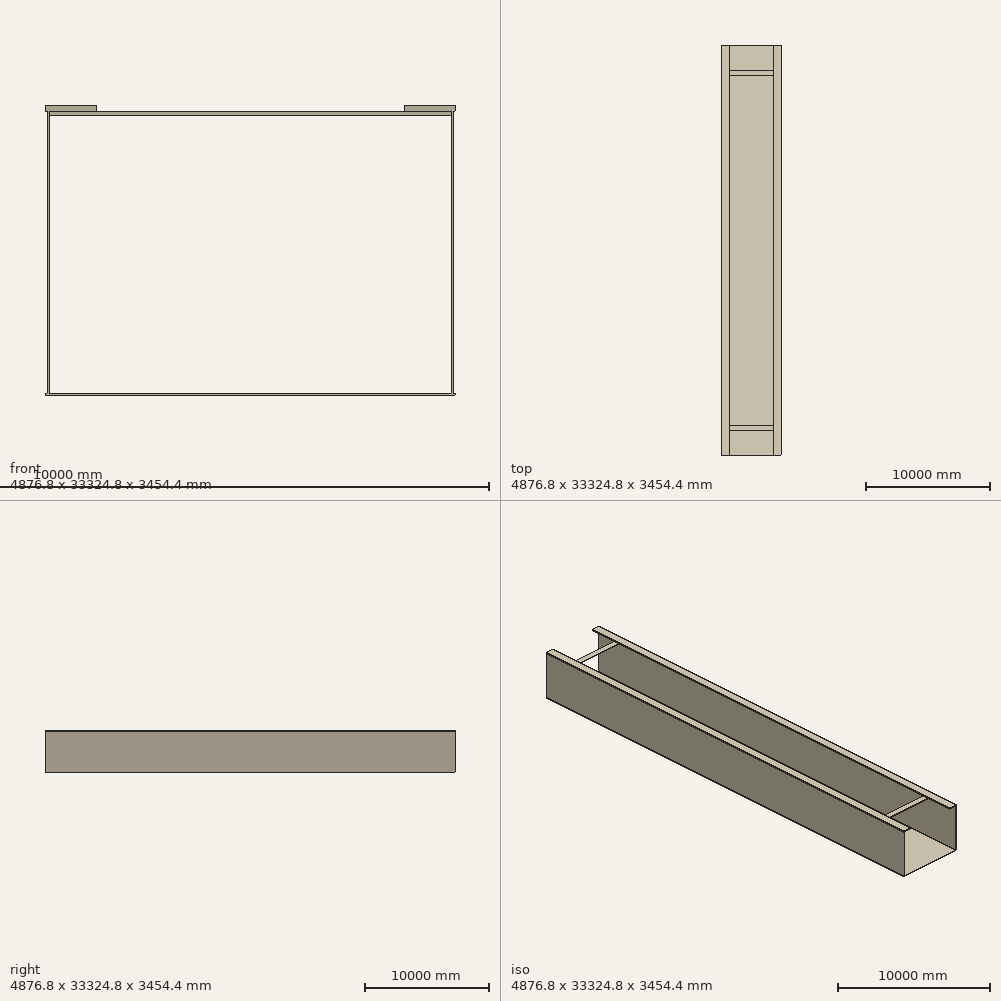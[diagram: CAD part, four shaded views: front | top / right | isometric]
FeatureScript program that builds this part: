
annotation { "Feature Type Name" : "Feature", "Feature Type Description" : "" }
export const myFeature = defineFeature(function(context is Context, id is Id, definition is map)
    precondition{}
    {
        {
            var Q0;
            Q0=qCreatedBy(makeId("Front.planeOp"),FACE);
            var sketch = newSketch(context, id + "F0", { "sketchPlane" : qUnion([Q0])});
            skLineSegment(sketch, "E0.bottom", {"start": v(0, 0) * mm, "end": v(4876.8, 0) * mm});
            skLineSegment(sketch, "E0.top", {"start": v(0, 25.4) * mm, "end": v(4876.8, 25.4) * mm});
            skLineSegment(sketch, "E0.left", {"start": v(0, 0) * mm, "end": v(0, 25.4) * mm});
            skLineSegment(sketch, "E0.right", {"start": v(4876.8, 0) * mm, "end": v(4876.8, 25.4) * mm});
            skLineSegment(sketch, "E1.left", {"start": v(4826, 25.4) * mm, "end": v(4826, 3378.2) * mm});
            skLineSegment(sketch, "E1.right", {"start": v(4851.4, 25.4) * mm, "end": v(4851.4, 3378.2) * mm});
            skLineSegment(sketch, "E2.bottom", {"start": v(25.4, 25.4) * mm, "end": v(50.8, 25.4) * mm});
            skLineSegment(sketch, "E2.top", {"start": v(25.4, 3378.2) * mm, "end": v(50.8, 3378.2) * mm});
            skLineSegment(sketch, "E2.left", {"start": v(25.4, 25.4) * mm, "end": v(25.4, 3378.2) * mm});
            skLineSegment(sketch, "E2.right", {"start": v(50.8, 25.4) * mm, "end": v(50.8, 3378.2) * mm});
            skLineSegment(sketch, "E3.bottom", {"start": v(0, 3378.2) * mm, "end": v(609.6, 3378.2) * mm});
            skLineSegment(sketch, "E3.top", {"start": v(0, 3454.4) * mm, "end": v(609.6, 3454.4) * mm});
            skLineSegment(sketch, "E3.left", {"start": v(0, 3378.2) * mm, "end": v(0, 3454.4) * mm});
            skLineSegment(sketch, "E3.right", {"start": v(4876.8, 3378.2) * mm, "end": v(4876.8, 3454.4) * mm});
            skLineSegment(sketch, "E4", {"start": v(609.6, 3454.4) * mm, "end": v(609.6, 3378.2) * mm});
            skLineSegment(sketch, "E5", {"start": v(4267.2, 3454.4) * mm, "end": v(4267.2, 3378.2) * mm});
            skLineSegment(sketch, "E6.trimOffspring", {"start": v(4267.2, 3454.4) * mm, "end": v(4876.8, 3454.4) * mm});
            skLineSegment(sketch, "E7.trimOffspring", {"start": v(4267.2, 3378.2) * mm, "end": v(4826, 3378.2) * mm});
            skLineSegment(sketch, "E8.trimOffspring", {"start": v(4851.4, 3378.2) * mm, "end": v(4876.8, 3378.2) * mm});
            skSolve(sketch);
        }
        {
            var Q0;
            Q0 = qSketchRegion(id + "F0", true);
            extrude(context, id + "F1", {"entities" : qUnion([Q0]), "depth" : 33324.8 * mm});
        }
        {
            var Q0;
            Q0=makeQuery(id+"F1.opExtrude","SWEPT_FACE",FACE,{"disambiguationData":[OSD([sQuery(id+"F0.wireOp",EDGE,"E2.right")])]});
            var sketch = newSketch(context, id + "F2", { "sketchPlane" : qUnion([Q0])});
            skLineSegment(sketch, "E9.bottom", {"start": v(-31276.75, 3378.2) * mm, "end": v(-30847.49, 3378.2) * mm});
            skLineSegment(sketch, "E9.top", {"start": v(-31276.75, 3327.4) * mm, "end": v(-30847.49, 3327.4) * mm});
            skLineSegment(sketch, "E9.left", {"start": v(-31276.75, 3378.2) * mm, "end": v(-31276.75, 3327.4) * mm});
            skLineSegment(sketch, "E9.right", {"start": v(-30847.49, 3378.2) * mm, "end": v(-30847.49, 3327.4) * mm});
            skLineSegment(sketch, "E10", {"start": v(-16662.4, 3378.2) * mm, "end": v(-16662.4, 2532.1) * mm});
            skLineSegment(sketch, "E11.MirrorCS", {"start": v(-2048.05, 3378.2) * mm, "end": v(-2477.31, 3378.2) * mm});
            skLineSegment(sketch, "E12.MirrorCS", {"start": v(-2048.05, 3327.4) * mm, "end": v(-2477.31, 3327.4) * mm});
            skLineSegment(sketch, "E13.MirrorCS", {"start": v(-2048.05, 3378.2) * mm, "end": v(-2048.05, 3327.4) * mm});
            skLineSegment(sketch, "E14.MirrorCS", {"start": v(-2477.31, 3378.2) * mm, "end": v(-2477.31, 3327.4) * mm});
            skSolve(sketch);
        }
        {
            var Q0;
            Q0 = qSketchRegion(id + "F2", true);
            var Q1;
            Q1=makeQuery(id+"F1.opExtrude","SWEPT_FACE",FACE,{"disambiguationData":[OSD([sQuery(id+"F0.wireOp",EDGE,"E1.left")])]});
            extrude(context, id + "F3", {"entities" : qUnion([Q0]), "operationType" : NewBodyOperationType.ADD, "endBound" : BoundingType.UP_TO_SURFACE, "endBoundEntityFace" : qUnion([Q1]), "depth" : 25.4 * mm});
        }
    });
